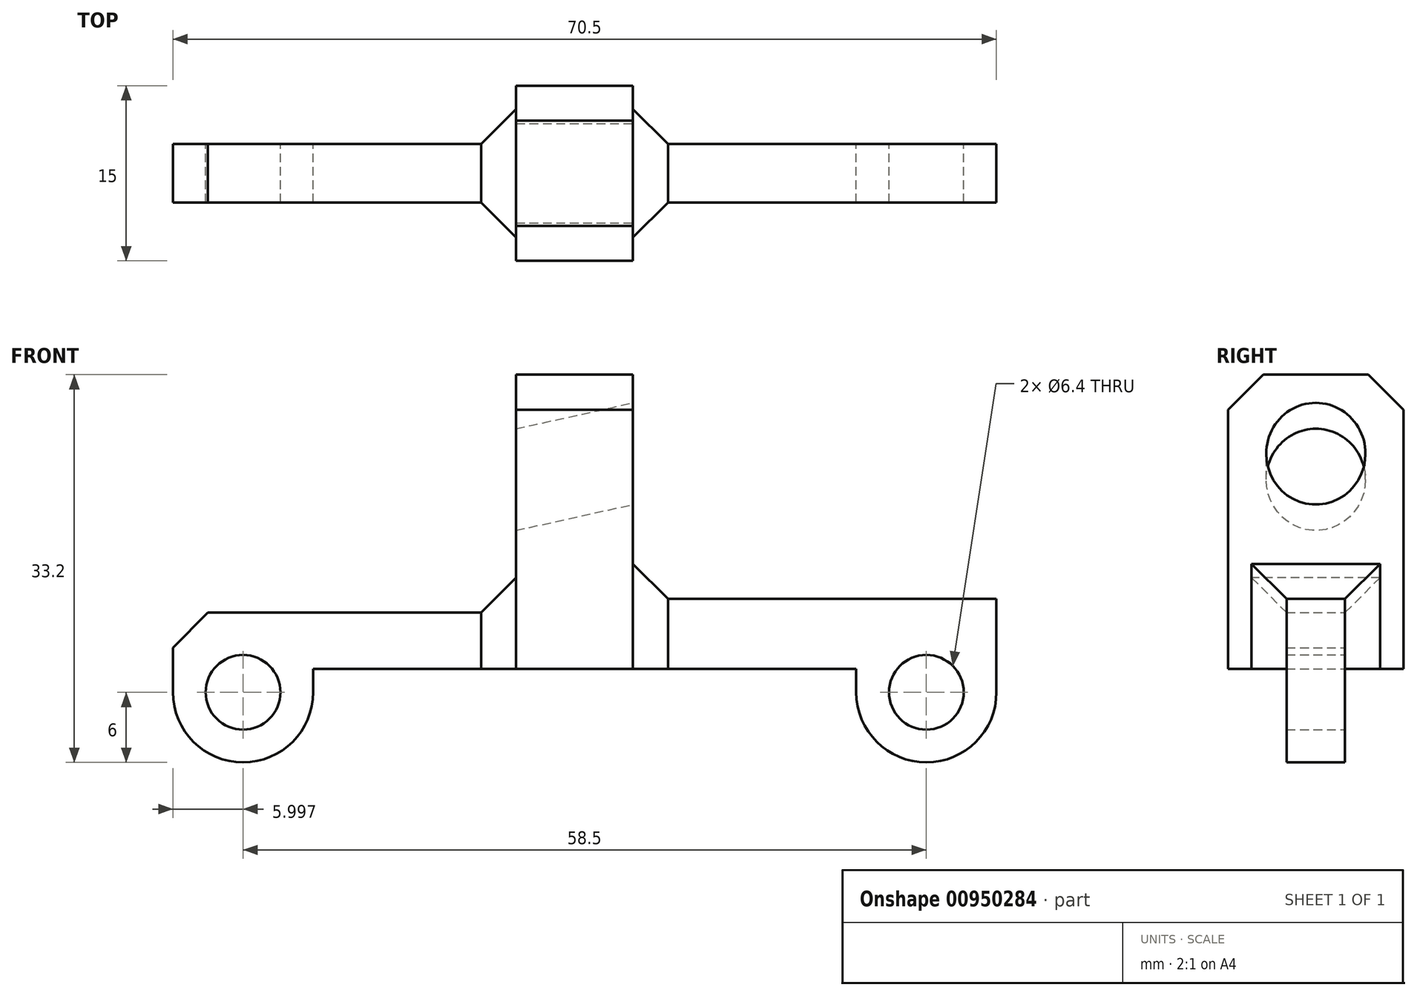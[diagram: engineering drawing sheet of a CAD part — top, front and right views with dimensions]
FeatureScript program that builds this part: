
annotation { "Feature Type Name" : "Feature", "Feature Type Description" : "" }
export const myFeature = defineFeature(function(context is Context, id is Id, definition is map)
    precondition{}
    {
        {
            var Q0;
            Q0=qCreatedBy(makeId("Top.planeOp"),FACE);
            var sketch = newSketch(context, id + "F0", { "sketchPlane" : qUnion([Q0])});
            skLineSegment(sketch, "E0.bottom", {"start": v(5, -7.5) * mm, "end": v(-5, -7.5) * mm});
            skLineSegment(sketch, "E0.top", {"start": v(5, 7.5) * mm, "end": v(-5, 7.5) * mm});
            skLineSegment(sketch, "E0.left", {"start": v(5, -7.5) * mm, "end": v(5, 7.5) * mm});
            skLineSegment(sketch, "E0.right", {"start": v(-5, -7.5) * mm, "end": v(-5, 7.5) * mm});
            skPoint(sketch, "E0.middle", {"position": v(0, 0) * mm});
            skSolve(sketch);
        }
        {
            var Q0;
            Q0 = qSketchRegion(id + "F0", true);
            extrude(context, id + "F1", {"entities" : qUnion([Q0]), "depth" : 25.2 * mm, "offsetDistance" : 25 * mm});
        }
        {
            var Q0;
            Q0=makeQuery(id+"F1.opExtrude","SWEPT_FACE",FACE,{"disambiguationData":[OSD([sQuery(id+"F0.wireOp",EDGE,"E0.left")])]});
            var sketch = newSketch(context, id + "F2", { "sketchPlane" : qUnion([Q0])});
            skLineSegment(sketch, "E1", {"start": v(20.23, 25.2) * mm, "end": v(-48.92, 25.2) * mm, "construction": true});
            skSolve(sketch);
        }
        {
            var Q0;
            Q0=sQuery(id+"F2.wireOp",EDGE,"E1");
            cPlane(context, id + "F3", {"entities" : qUnion([Q0]), "cplaneType" : CPlaneType.LINE_ANGLE, "offset" : 25 * mm, "angle" : 102.5 * degree, "width" : 150 * mm, "height" : 150 * mm});
        }
        {
            var Q0;
            Q0=qCreatedBy(id+"F3.planeOp",FACE);
            var sketch = newSketch(context, id + "F4", { "sketchPlane" : qUnion([Q0])});
            skCircle(sketch, "E2", {"center": v(0, 16.92) * mm, "radius": 4.25 * mm});
            skSolve(sketch);
        }
        {
            var Q0;
            Q0 = qSketchRegion(id + "F4", true);
            extrude(context, id + "F5", {"entities" : qUnion([Q0]), "operationType" : NewBodyOperationType.REMOVE, "oppositeDirection" : true, "depth" : 25 * mm, "offsetDistance" : 25 * mm});
        }
        {
            var Q0;
            Q0=qCreatedBy(makeId("Front.planeOp"),FACE);
            var sketch = newSketch(context, id + "F6", { "sketchPlane" : qUnion([Q0])});
            skCircle(sketch, "E3", {"center": v(-28.37, -2) * mm, "radius": 3.2 * mm});
            skCircle(sketch, "E4", {"center": v(30.13, -2) * mm, "radius": 3.2 * mm});
            skCircle(sketch, "E5", {"center": v(-28.37, -2) * mm, "radius": 6 * mm});
            skCircle(sketch, "E6", {"center": v(30.13, -2) * mm, "radius": 6 * mm});
            skLineSegment(sketch, "E7", {"start": v(-22.37, -2) * mm, "end": v(-22.37, 0) * mm});
            skLineSegment(sketch, "E8", {"start": v(36.13, -2) * mm, "end": v(36.13, 3.48) * mm});
            skLineSegment(sketch, "E9", {"start": v(-34.37, 3.48) * mm, "end": v(-34.37, -2) * mm});
            skLineSegment(sketch, "E10", {"start": v(4.55, 6) * mm, "end": v(39.22, 6) * mm});
            skLineSegment(sketch, "E11", {"start": v(24.13, 0) * mm, "end": v(24.13, -2) * mm});
            skLineSegment(sketch, "E12", {"start": v(51.63, -2) * mm, "end": v(-39.41, -2) * mm, "construction": true});
            skLineSegment(sketch, "E13.trimOffspring", {"start": v(-22.37, 0) * mm, "end": v(24.13, 0) * mm});
            skLineSegment(sketch, "E14", {"start": v(-34.37, 3.48) * mm, "end": v(-34.37, 4.82) * mm});
            skLineSegment(sketch, "E15", {"start": v(-34.37, 4.82) * mm, "end": v(4.32, 4.82) * mm});
            skLineSegment(sketch, "E16", {"start": v(4.55, 6) * mm, "end": v(4.32, 4.82) * mm});
            skLineSegment(sketch, "E17", {"start": v(36.13, 3.48) * mm, "end": v(36.13, 6) * mm});
            skSolve(sketch);
        }
        {
            var Q0;
            Q0 = qSketchRegion(id + "F6", true);
            extrude(context, id + "F7", {"entities" : qUnion([Q0]), "operationType" : NewBodyOperationType.ADD, "endBound" : BoundingType.SYMMETRIC, "depth" : 5 * mm, "offsetDistance" : 25 * mm});
        }
        {
            var Q0;
            Q0=makeQuery(id+"F7.boolean.opBoolean","INTERSECT",EDGE,{"derivedFrom":[makeQuery(id+"F1.opExtrude","SWEPT_FACE",FACE,{"disambiguationData":[OSD([sQuery(id+"F0.wireOp",EDGE,"E0.right")])]}),makeQuery(id+"F7.opExtrude","SWEPT_FACE",FACE,{"disambiguationData":[OSD([sQuery(id+"F6.wireOp",EDGE,"E15")])]})]});
            var Q1;
            Q1=makeQuery(id+"F7.boolean.opBoolean","INTERSECT",EDGE,{"derivedFrom":[makeQuery(id+"F1.opExtrude","SWEPT_FACE",FACE,{"disambiguationData":[OSD([sQuery(id+"F0.wireOp",EDGE,"E0.left")])]}),makeQuery(id+"F7.opExtrude","SWEPT_FACE",FACE,{"disambiguationData":[OSD([sQuery(id+"F6.wireOp",EDGE,"E10")])]})]});
            var Q2;
            Q2=makeQuery(id+"F1.opExtrude","CAP_EDGE",EDGE,{"disambiguationData":[OSD([sQuery(id+"F0.wireOp",EDGE,"E0.bottom")])],"isStart":false});
            var Q3;
            Q3=makeQuery(id+"F1.opExtrude","CAP_EDGE",EDGE,{"disambiguationData":[OSD([sQuery(id+"F0.wireOp",EDGE,"E0.top")])],"isStart":false});
            var Q4;
            Q4=makeQuery(id+"F7.boolean.opBoolean","INTERSECT",EDGE,{"derivedFrom":[makeQuery(id+"F1.opExtrude","SWEPT_FACE",FACE,{"disambiguationData":[OSD([sQuery(id+"F0.wireOp",EDGE,"E0.left")])]}),makeQuery(id+"F7.opExtrude","CAP_FACE",FACE,{"disambiguationData":[OSD([sQuery(id+"F6.wireOp",EDGE,"E3"),sQuery(id+"F6.wireOp",EDGE,"E4"),sQuery(id+"F6.wireOp",EDGE,"E5"),sQuery(id+"F6.wireOp",EDGE,"E6"),sQuery(id+"F6.wireOp",EDGE,"E7"),sQuery(id+"F6.wireOp",EDGE,"E8"),sQuery(id+"F6.wireOp",EDGE,"E9"),sQuery(id+"F6.wireOp",EDGE,"E10"),sQuery(id+"F6.wireOp",EDGE,"EudRBZE3-9ySA-ByuQ-Sp4c-DmzhYLhN9UEo"),sQuery(id+"F6.wireOp",EDGE,"E11"),sQuery(id+"F6.wireOp",EDGE,"E13.trimOffspring"),sQuery(id+"F6.wireOp",EDGE,"E14"),sQuery(id+"F6.wireOp",EDGE,"E15"),sQuery(id+"F6.wireOp",EDGE,"E16")])],"isStart":false})]});
            var Q5;
            Q5=makeQuery(id+"F7.boolean.opBoolean","INTERSECT",EDGE,{"derivedFrom":[makeQuery(id+"F1.opExtrude","SWEPT_FACE",FACE,{"disambiguationData":[OSD([sQuery(id+"F0.wireOp",EDGE,"E0.left")])]}),makeQuery(id+"F7.opExtrude","CAP_FACE",FACE,{"disambiguationData":[OSD([sQuery(id+"F6.wireOp",EDGE,"E3"),sQuery(id+"F6.wireOp",EDGE,"E4"),sQuery(id+"F6.wireOp",EDGE,"E5"),sQuery(id+"F6.wireOp",EDGE,"E6"),sQuery(id+"F6.wireOp",EDGE,"E7"),sQuery(id+"F6.wireOp",EDGE,"E8"),sQuery(id+"F6.wireOp",EDGE,"E9"),sQuery(id+"F6.wireOp",EDGE,"E10"),sQuery(id+"F6.wireOp",EDGE,"EudRBZE3-9ySA-ByuQ-Sp4c-DmzhYLhN9UEo"),sQuery(id+"F6.wireOp",EDGE,"E11"),sQuery(id+"F6.wireOp",EDGE,"E13.trimOffspring"),sQuery(id+"F6.wireOp",EDGE,"E14"),sQuery(id+"F6.wireOp",EDGE,"E15"),sQuery(id+"F6.wireOp",EDGE,"E16")])],"isStart":true})]});
            var Q6;
            Q6=makeQuery(id+"F7.boolean.opBoolean","INTERSECT",EDGE,{"derivedFrom":[makeQuery(id+"F1.opExtrude","SWEPT_FACE",FACE,{"disambiguationData":[OSD([sQuery(id+"F0.wireOp",EDGE,"E0.right")])]}),makeQuery(id+"F7.opExtrude","CAP_FACE",FACE,{"disambiguationData":[OSD([sQuery(id+"F6.wireOp",EDGE,"E3"),sQuery(id+"F6.wireOp",EDGE,"E4"),sQuery(id+"F6.wireOp",EDGE,"E5"),sQuery(id+"F6.wireOp",EDGE,"E6"),sQuery(id+"F6.wireOp",EDGE,"E7"),sQuery(id+"F6.wireOp",EDGE,"E8"),sQuery(id+"F6.wireOp",EDGE,"E9"),sQuery(id+"F6.wireOp",EDGE,"E10"),sQuery(id+"F6.wireOp",EDGE,"EudRBZE3-9ySA-ByuQ-Sp4c-DmzhYLhN9UEo"),sQuery(id+"F6.wireOp",EDGE,"E11"),sQuery(id+"F6.wireOp",EDGE,"E13.trimOffspring"),sQuery(id+"F6.wireOp",EDGE,"E14"),sQuery(id+"F6.wireOp",EDGE,"E15"),sQuery(id+"F6.wireOp",EDGE,"E16")])],"isStart":true})]});
            var Q7;
            Q7=makeQuery(id+"F7.boolean.opBoolean","INTERSECT",EDGE,{"derivedFrom":[makeQuery(id+"F1.opExtrude","SWEPT_FACE",FACE,{"disambiguationData":[OSD([sQuery(id+"F0.wireOp",EDGE,"E0.right")])]}),makeQuery(id+"F7.opExtrude","CAP_FACE",FACE,{"disambiguationData":[OSD([sQuery(id+"F6.wireOp",EDGE,"E3"),sQuery(id+"F6.wireOp",EDGE,"E4"),sQuery(id+"F6.wireOp",EDGE,"E5"),sQuery(id+"F6.wireOp",EDGE,"E6"),sQuery(id+"F6.wireOp",EDGE,"E7"),sQuery(id+"F6.wireOp",EDGE,"E8"),sQuery(id+"F6.wireOp",EDGE,"E9"),sQuery(id+"F6.wireOp",EDGE,"E10"),sQuery(id+"F6.wireOp",EDGE,"EudRBZE3-9ySA-ByuQ-Sp4c-DmzhYLhN9UEo"),sQuery(id+"F6.wireOp",EDGE,"E11"),sQuery(id+"F6.wireOp",EDGE,"E13.trimOffspring"),sQuery(id+"F6.wireOp",EDGE,"E14"),sQuery(id+"F6.wireOp",EDGE,"E15"),sQuery(id+"F6.wireOp",EDGE,"E16")])],"isStart":false})]});
            var Q8;
            Q8=makeQuery(id+"F7.opExtrude","SWEPT_EDGE",EDGE,{"disambiguationData":[OSD([sQuery(id+"F6.wireOp",EDGE,"E14"),sQuery(id+"F6.wireOp",EDGE,"E15")])]});
            chamfer(context, id + "F8", {"entities" : qUnion([Q0, Q1, Q2, Q3, Q4, Q5, Q6, Q7, Q8]), "width" : 3 * mm, "tangentPropagation" : true});
        }
    });
